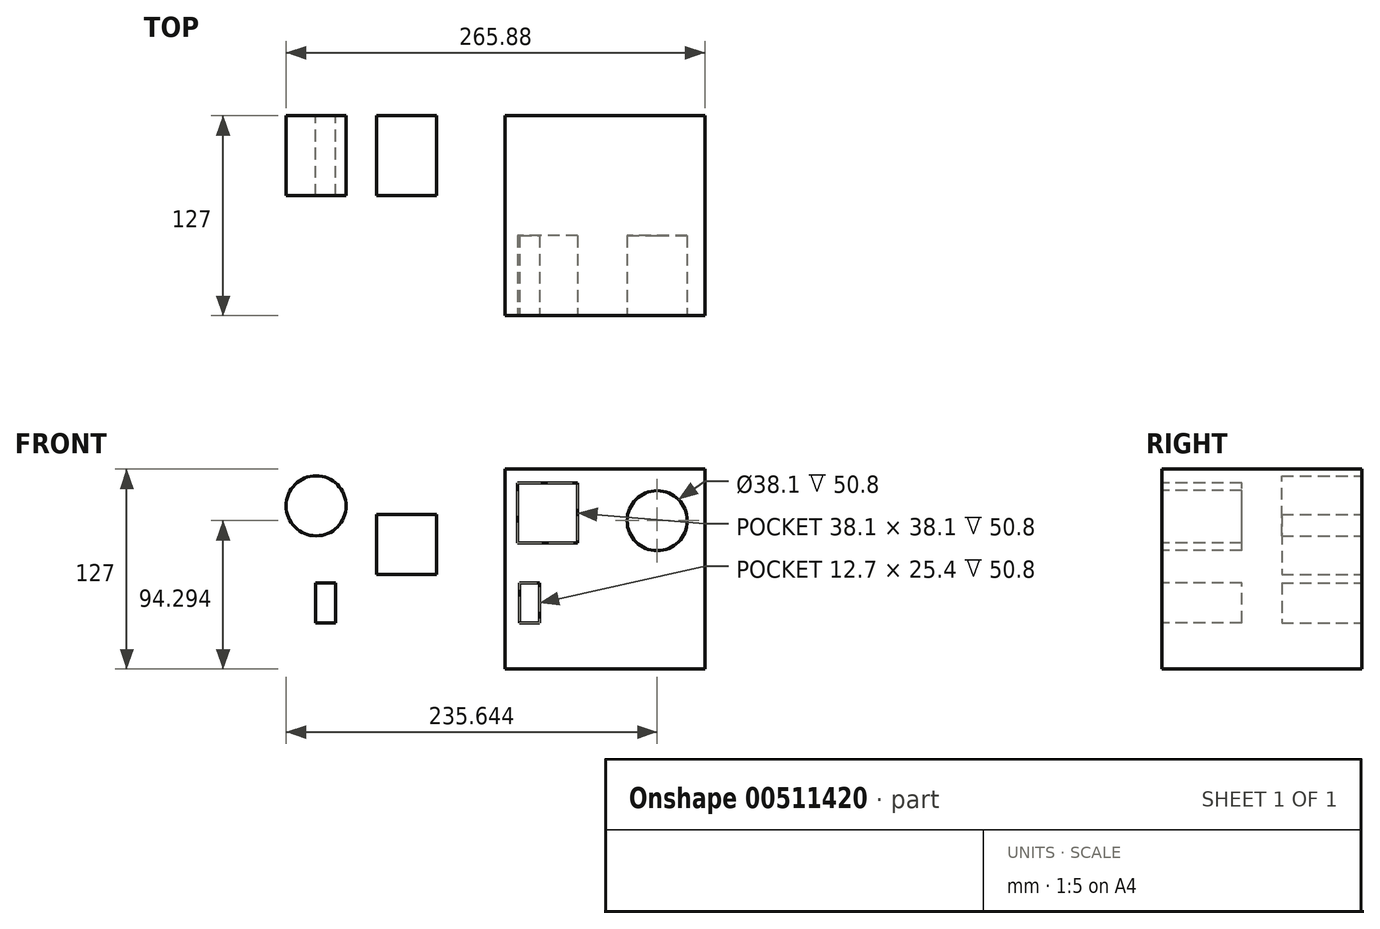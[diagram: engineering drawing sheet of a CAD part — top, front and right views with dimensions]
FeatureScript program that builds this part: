
annotation { "Feature Type Name" : "Feature", "Feature Type Description" : "" }
export const myFeature = defineFeature(function(context is Context, id is Id, definition is map)
    precondition{}
    {
        {
            var Q0;
            Q0=qCreatedBy(makeId("Front.planeOp"),FACE);
            var sketch = newSketch(context, id + "F0", { "sketchPlane" : qUnion([Q0])});
            skLineSegment(sketch, "E0.bottom", {"start": v(-63.5, 63.5) * mm, "end": v(63.5, 63.5) * mm});
            skLineSegment(sketch, "E0.top", {"start": v(-63.5, -63.5) * mm, "end": v(63.5, -63.5) * mm});
            skLineSegment(sketch, "E0.left", {"start": v(-63.5, 63.5) * mm, "end": v(-63.5, -63.5) * mm});
            skLineSegment(sketch, "E0.right", {"start": v(63.5, 63.5) * mm, "end": v(63.5, -63.5) * mm});
            skPoint(sketch, "E0.middle", {"position": v(0, 0) * mm});
            skSolve(sketch);
        }
        {
            var Q0;
            Q0=makeQuery(id+"F0.imprint","IMPRINT",FACE,{"disambiguationData":[TD([[makeQuery(id+"F0.imprint","IMPRINT",EDGE,{"derivedFrom":sQuery(id+"F0.wireOp",EDGE,"E0.bottom")}),-1.0]])]});
            extrude(context, id + "F1", {"entities" : qUnion([Q0]), "depth" : 127 * mm});
        }
        {
            var Q0;
            Q0=makeQuery(id+"F1.opExtrude","CAP_FACE",FACE,{"disambiguationData":[OSD([sQuery(id+"F0.wireOp",EDGE,"E0.bottom"),sQuery(id+"F0.wireOp",EDGE,"E0.top"),sQuery(id+"F0.wireOp",EDGE,"E0.left"),sQuery(id+"F0.wireOp",EDGE,"E0.right")])],"isStart":false});
            var sketch = newSketch(context, id + "F2", { "sketchPlane" : qUnion([Q0])});
            skLineSegment(sketch, "E1.bottom", {"start": v(-17.2, 16.7) * mm, "end": v(-55.3, 16.7) * mm});
            skLineSegment(sketch, "E1.top", {"start": v(-17.2, 54.8) * mm, "end": v(-55.3, 54.8) * mm});
            skLineSegment(sketch, "E1.left", {"start": v(-17.2, 16.7) * mm, "end": v(-17.2, 54.8) * mm});
            skLineSegment(sketch, "E1.right", {"start": v(-55.3, 16.7) * mm, "end": v(-55.3, 54.8) * mm});
            skPoint(sketch, "E1.middle", {"position": v(-36.24, 35.75) * mm});
            skSolve(sketch);
        }
        {
            var Q0;
            Q0=makeQuery(id+"F2.imprint","IMPRINT",FACE,{"disambiguationData":[TD([[makeQuery(id+"F2.imprint","IMPRINT",EDGE,{"derivedFrom":sQuery(id+"F2.wireOp",EDGE,"E1.bottom")}),-1.0]])]});
            extrude(context, id + "F3", {"entities" : qUnion([Q0]), "operationType" : NewBodyOperationType.REMOVE, "oppositeDirection" : true, "depth" : 50.8 * mm, "offsetDistance" : 25.4 * mm});
        }
        {
            var Q0;
            Q0=makeQuery(id+"F1.opExtrude","CAP_FACE",FACE,{"disambiguationData":[OSD([sQuery(id+"F0.wireOp",EDGE,"E0.bottom"),sQuery(id+"F0.wireOp",EDGE,"E0.top"),sQuery(id+"F0.wireOp",EDGE,"E0.left"),sQuery(id+"F0.wireOp",EDGE,"E0.right")])],"isStart":false});
            var sketch = newSketch(context, id + "F4", { "sketchPlane" : qUnion([Q0])});
            skCircle(sketch, "E2", {"center": v(33.26, 30.8) * mm, "radius": 19.05 * mm});
            skSolve(sketch);
        }
        {
            var Q0;
            Q0=makeQuery(id+"F4.imprint","IMPRINT",FACE,{"disambiguationData":[TD([[makeQuery(id+"F4.imprint","IMPRINT",EDGE,{"derivedFrom":sQuery(id+"F4.wireOp",EDGE,"E2")}),1.0]])]});
            extrude(context, id + "F5", {"entities" : qUnion([Q0]), "operationType" : NewBodyOperationType.REMOVE, "oppositeDirection" : true, "depth" : 50.8 * mm, "offsetDistance" : 25.4 * mm});
        }
        {
            var Q0;
            Q0=makeQuery(id+"F1.opExtrude","CAP_FACE",FACE,{"disambiguationData":[OSD([sQuery(id+"F0.wireOp",EDGE,"E0.bottom"),sQuery(id+"F0.wireOp",EDGE,"E0.top"),sQuery(id+"F0.wireOp",EDGE,"E0.left"),sQuery(id+"F0.wireOp",EDGE,"E0.right")])],"isStart":false});
            var sketch = newSketch(context, id + "F6", { "sketchPlane" : qUnion([Q0])});
            skLineSegment(sketch, "E3.bottom", {"start": v(-54.14, -34.03) * mm, "end": v(-41.44, -34.03) * mm});
            skLineSegment(sketch, "E3.top", {"start": v(-54.14, -8.63) * mm, "end": v(-41.44, -8.63) * mm});
            skLineSegment(sketch, "E3.left", {"start": v(-54.14, -34.03) * mm, "end": v(-54.14, -8.63) * mm});
            skLineSegment(sketch, "E3.right", {"start": v(-41.44, -34.03) * mm, "end": v(-41.44, -8.63) * mm});
            skPoint(sketch, "E3.middle", {"position": v(-47.79, -21.33) * mm});
            skSolve(sketch);
        }
        {
            var Q0;
            Q0=makeQuery(id+"F6.imprint","IMPRINT",FACE,{"disambiguationData":[TD([[makeQuery(id+"F6.imprint","IMPRINT",EDGE,{"derivedFrom":sQuery(id+"F6.wireOp",EDGE,"E3.bottom")}),1.0]])]});
            extrude(context, id + "F7", {"entities" : qUnion([Q0]), "operationType" : NewBodyOperationType.REMOVE, "depth" : -50.8 * mm, "offsetDistance" : 25.4 * mm});
        }
        {
            var Q0;
            Q0=qCreatedBy(makeId("Front.planeOp"),FACE);
            var sketch = newSketch(context, id + "F8", { "sketchPlane" : qUnion([Q0])});
            skLineSegment(sketch, "E4.bottom", {"start": v(-144.93, 34.66) * mm, "end": v(-106.83, 34.66) * mm});
            skLineSegment(sketch, "E4.top", {"start": v(-144.93, -3.44) * mm, "end": v(-106.83, -3.44) * mm});
            skLineSegment(sketch, "E4.left", {"start": v(-144.93, 34.66) * mm, "end": v(-144.93, -3.44) * mm});
            skLineSegment(sketch, "E4.right", {"start": v(-106.83, 34.66) * mm, "end": v(-106.83, -3.44) * mm});
            skSolve(sketch);
        }
        {
            var Q0;
            Q0=makeQuery(id+"F8.imprint","IMPRINT",FACE,{"disambiguationData":[TD([[makeQuery(id+"F8.imprint","IMPRINT",EDGE,{"derivedFrom":sQuery(id+"F8.wireOp",EDGE,"E4.bottom")}),-1.0]])]});
            var Q1;
            Q1=makeQuery(id+"F5.boolean.opBoolean","COPY",FACE,{"derivedFrom":makeQuery(id+"F5.opExtrude","CAP_FACE",FACE,{"disambiguationData":[OSD([sQuery(id+"F4.wireOp",EDGE,"E2")])],"isStart":false})});
            extrude(context, id + "F9", {"entities" : qUnion([Q0, Q1]), "depth" : 50.8 * mm, "offsetDistance" : 25.4 * mm});
        }
        {
            var Q0;
            Q0=makeQuery(id+"F9.opExtrude","CAP_FACE",FACE,{"disambiguationData":[OSD([sQuery(id+"F4.wireOp",EDGE,"E2")])],"isStart":false});
            extrude(context, id + "F10", {"entities" : qUnion([Q0]), "operationType" : NewBodyOperationType.REMOVE, "oppositeDirection" : true, "depth" : 50.8 * mm, "offsetDistance" : 25.4 * mm});
        }
        {
            var Q0;
            Q0=qCreatedBy(makeId("Front.planeOp"),FACE);
            var sketch = newSketch(context, id + "F11", { "sketchPlane" : qUnion([Q0])});
            skCircle(sketch, "E5", {"center": v(-183.33, 40.2) * mm, "radius": 19.05 * mm});
            skSolve(sketch);
        }
        {
            var Q0;
            Q0=makeQuery(id+"F11.imprint","IMPRINT",FACE,{"disambiguationData":[TD([[makeQuery(id+"F11.imprint","IMPRINT",EDGE,{"derivedFrom":sQuery(id+"F11.wireOp",EDGE,"E5")}),1.0]])]});
            extrude(context, id + "F12", {"entities" : qUnion([Q0]), "depth" : 50.8 * mm, "offsetDistance" : 25.4 * mm});
        }
        {
            var Q0;
            Q0=qCreatedBy(makeId("Front.planeOp"),FACE);
            var sketch = newSketch(context, id + "F13", { "sketchPlane" : qUnion([Q0])});
            skLineSegment(sketch, "E6.bottom", {"start": v(-183.57, -8.67) * mm, "end": v(-170.87, -8.67) * mm});
            skLineSegment(sketch, "E6.top", {"start": v(-183.57, -34.07) * mm, "end": v(-170.87, -34.07) * mm});
            skLineSegment(sketch, "E6.left", {"start": v(-183.57, -8.67) * mm, "end": v(-183.57, -34.07) * mm});
            skLineSegment(sketch, "E6.right", {"start": v(-170.87, -8.67) * mm, "end": v(-170.87, -34.07) * mm});
            skSolve(sketch);
        }
        {
            var Q0;
            Q0=makeQuery(id+"F13.imprint","IMPRINT",FACE,{"disambiguationData":[TD([[makeQuery(id+"F13.imprint","IMPRINT",EDGE,{"derivedFrom":sQuery(id+"F13.wireOp",EDGE,"E6.bottom")}),-1.0]])]});
            extrude(context, id + "F14", {"entities" : qUnion([Q0]), "depth" : 50.8 * mm, "offsetDistance" : 25.4 * mm});
        }
    });
